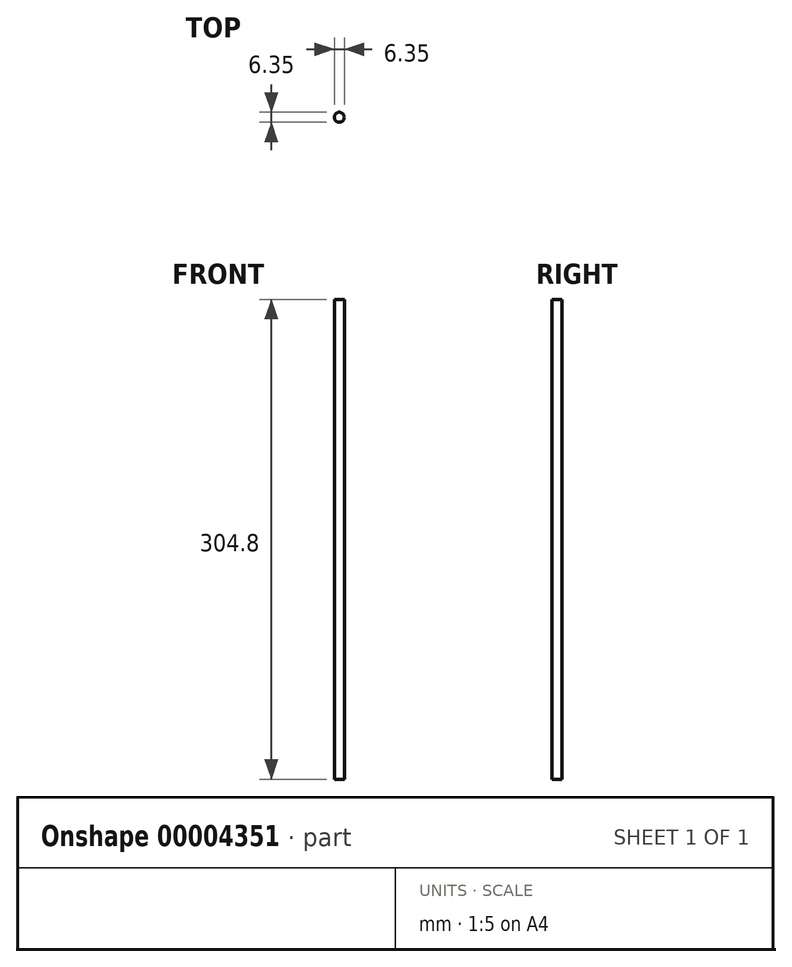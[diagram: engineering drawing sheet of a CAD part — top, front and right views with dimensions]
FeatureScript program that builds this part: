
annotation { "Feature Type Name" : "Feature", "Feature Type Description" : "" }
export const myFeature = defineFeature(function(context is Context, id is Id, definition is map)
    precondition{}
    {
        {
            var Q0;
            Q0=qCreatedBy(makeId("Top.planeOp"),FACE);
            var sketch = newSketch(context, id + "F0", { "sketchPlane" : qUnion([Q0])});
            skCircle(sketch, "E0", {"center": v(34.08, -44.01) * mm, "radius": 3.18 * mm});
            skSolve(sketch);
        }
        {
            var Q0;
            Q0 = qSketchRegion(id + "F0", true);
            extrude(context, id + "F1", {"entities" : qUnion([Q0]), "depth" : 304.8 * mm});
        }
    });
